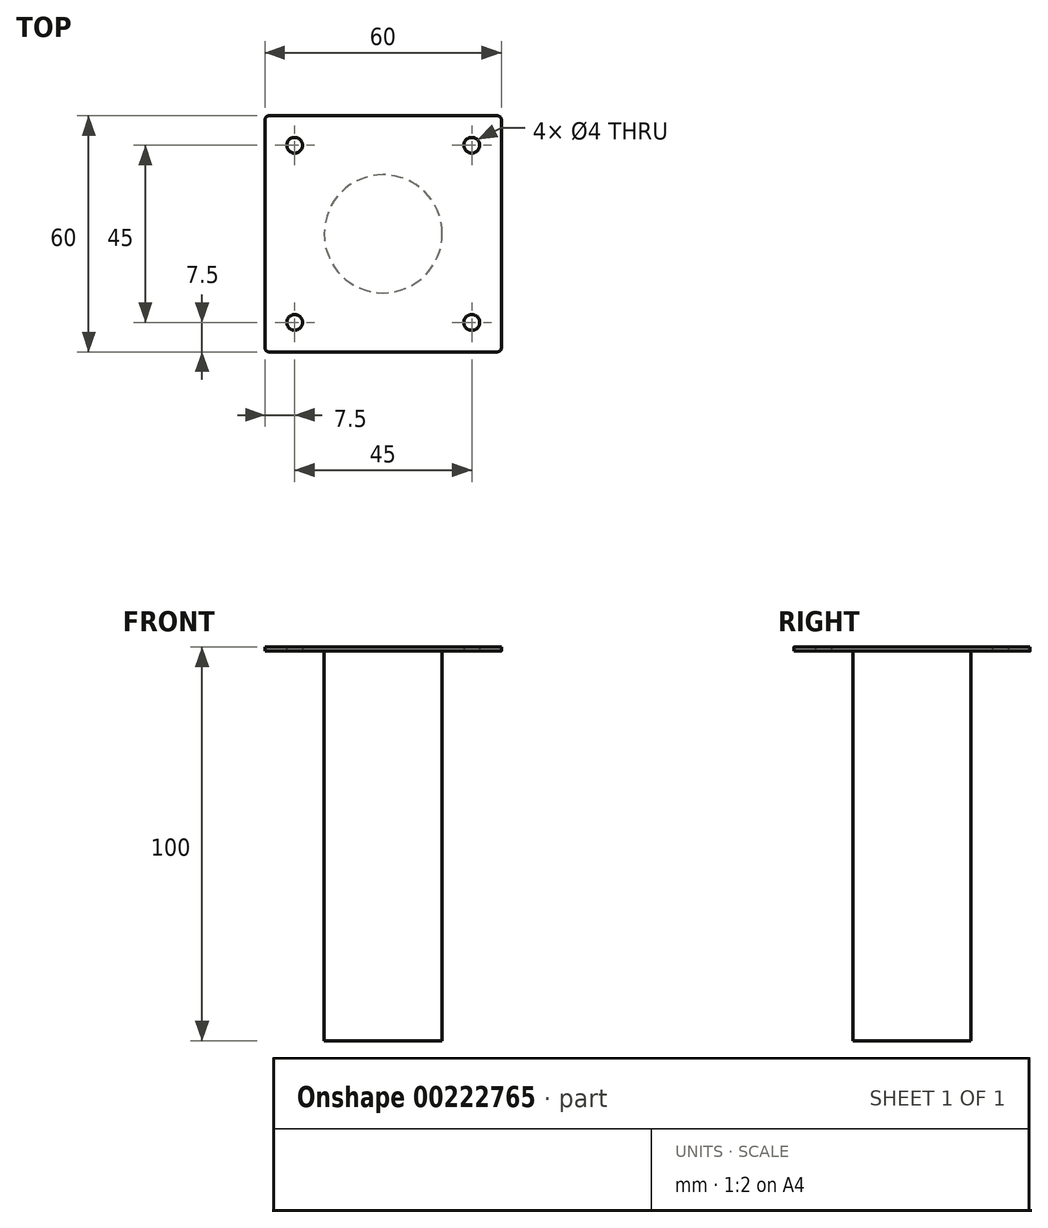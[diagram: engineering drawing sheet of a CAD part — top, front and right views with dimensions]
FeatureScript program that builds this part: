
annotation { "Feature Type Name" : "Feature", "Feature Type Description" : "" }
export const myFeature = defineFeature(function(context is Context, id is Id, definition is map)
    precondition{}
    {
        {
            var Q0;
            Q0=qCreatedBy(makeId("Top.planeOp"),FACE);
            var sketch = newSketch(context, id + "F0", { "sketchPlane" : qUnion([Q0])});
            skLineSegment(sketch, "E0.bottom", {"start": v(-29, -30) * mm, "end": v(29, -30) * mm});
            skLineSegment(sketch, "E0.top", {"start": v(-29, 30) * mm, "end": v(29, 30) * mm});
            skLineSegment(sketch, "E0.left", {"start": v(-30, -29) * mm, "end": v(-30, 29) * mm});
            skLineSegment(sketch, "E0.right", {"start": v(30, -29) * mm, "end": v(30, 29) * mm});
            skPoint(sketch, "E0.middle", {"position": v(0, 0) * mm});
            skLineSegment(sketch, "E1", {"start": v(-30, -22.5) * mm, "end": v(30, -22.5) * mm, "construction": true});
            skLineSegment(sketch, "E2", {"start": v(-22.5, -30) * mm, "end": v(-22.5, 30) * mm, "construction": true});
            skLineSegment(sketch, "E3", {"start": v(-30, 22.5) * mm, "end": v(30, 22.5) * mm, "construction": true});
            skLineSegment(sketch, "E4", {"start": v(22.5, -30) * mm, "end": v(22.5, 30) * mm, "construction": true});
            skPoint(sketch, "E5.visualSharp", {"position": v(-30, -30) * mm});
            skArc(sketch, "E5.filletArc", {"start": v(-30, -29) * mm, "mid": v(-29.7, -29.7) * mm, "end": v(-29, -30) * mm});
            skPoint(sketch, "E6.visualSharp", {"position": v(30, -30) * mm});
            skArc(sketch, "E6.filletArc", {"start": v(29, -30) * mm, "mid": v(29.7, -29.7) * mm, "end": v(30, -29) * mm});
            skPoint(sketch, "E7.visualSharp", {"position": v(30, 30) * mm});
            skArc(sketch, "E7.filletArc", {"start": v(30, 29) * mm, "mid": v(29.7, 29.7) * mm, "end": v(29, 30) * mm});
            skPoint(sketch, "E8.visualSharp", {"position": v(-30, 30) * mm});
            skArc(sketch, "E8.filletArc", {"start": v(-29, 30) * mm, "mid": v(-29.7, 29.7) * mm, "end": v(-30, 29) * mm});
            skCircle(sketch, "E9", {"center": v(-22.5, -22.5) * mm, "radius": 2 * mm});
            skCircle(sketch, "E10", {"center": v(22.5, -22.5) * mm, "radius": 2 * mm});
            skCircle(sketch, "E11", {"center": v(-22.5, 22.5) * mm, "radius": 2 * mm});
            skCircle(sketch, "E12", {"center": v(22.5, 22.5) * mm, "radius": 2 * mm});
            skSolve(sketch);
        }
        {
            var Q0;
            Q0=makeQuery(id+"F0.imprint","IMPRINT",FACE,{"disambiguationData":[TD([[makeQuery(id+"F0.imprint","IMPRINT",EDGE,{"derivedFrom":sQuery(id+"F0.wireOp",EDGE,"E0.bottom")}),1.0]])]});
            extrude(context, id + "F1", {"entities" : qUnion([Q0]), "depth" : 1 * mm});
        }
        {
            var Q0;
            Q0=makeQuery(id+"F1.opExtrude","CAP_FACE",FACE,{"disambiguationData":[OSD([sQuery(id+"F0.wireOp",EDGE,"E0.bottom"),sQuery(id+"F0.wireOp",EDGE,"E0.top"),sQuery(id+"F0.wireOp",EDGE,"E0.left"),sQuery(id+"F0.wireOp",EDGE,"E0.right"),sQuery(id+"F0.wireOp",EDGE,"E5.filletArc"),sQuery(id+"F0.wireOp",EDGE,"E6.filletArc"),sQuery(id+"F0.wireOp",EDGE,"E7.filletArc"),sQuery(id+"F0.wireOp",EDGE,"E8.filletArc"),sQuery(id+"F0.wireOp",EDGE,"E9"),sQuery(id+"F0.wireOp",EDGE,"E10"),sQuery(id+"F0.wireOp",EDGE,"E11"),sQuery(id+"F0.wireOp",EDGE,"E12")])],"isStart":true});
            var sketch = newSketch(context, id + "F2", { "sketchPlane" : qUnion([Q0])});
            skCircle(sketch, "E13", {"center": v(0, 0) * mm, "radius": 15 * mm});
            skSolve(sketch);
        }
        {
            var Q0;
            Q0=qSketchRegion(id+"F2",true);
            extrude(context, id + "F3", {"entities" : qUnion([Q0]), "operationType" : NewBodyOperationType.ADD, "depth" : 99 * mm});
        }
    });
